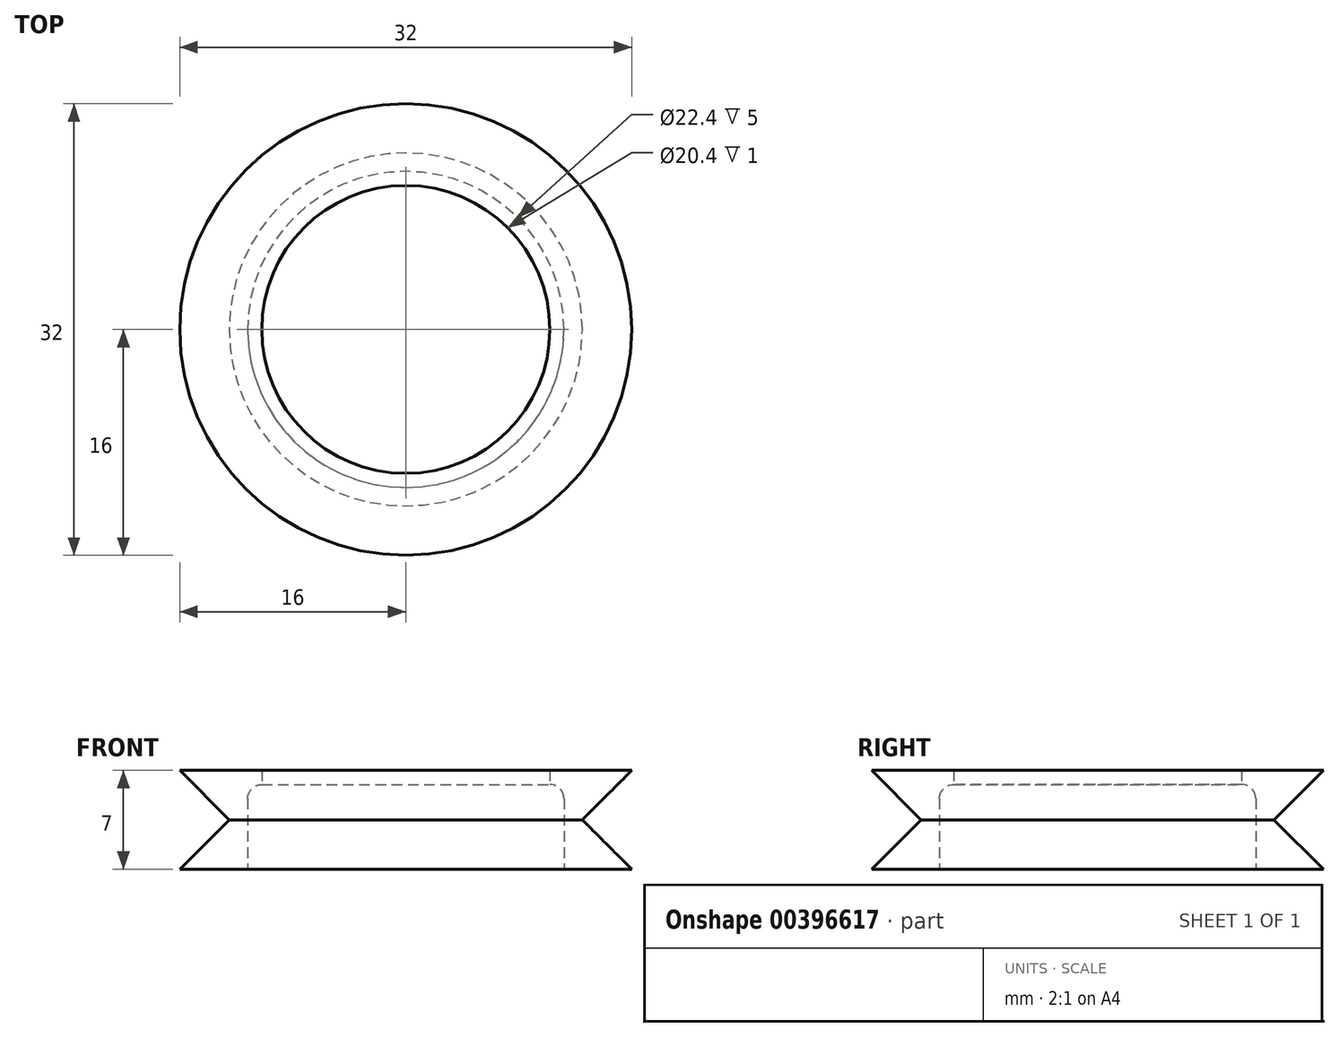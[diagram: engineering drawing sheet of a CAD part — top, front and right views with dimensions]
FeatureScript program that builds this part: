
annotation { "Feature Type Name" : "Feature", "Feature Type Description" : "" }
export const myFeature = defineFeature(function(context is Context, id is Id, definition is map)
    precondition{}
    {
        {
            var Q0;
            Q0=qCreatedBy(makeId("Front.planeOp"),FACE);
            var sketch = newSketch(context, id + "F0", { "sketchPlane" : qUnion([Q0])});
            skLineSegment(sketch, "E0.bottom", {"start": v(0, 13.24) * mm, "end": v(0, 13.24) * mm});
            skLineSegment(sketch, "E0.top", {"start": v(0, -13.74) * mm, "end": v(0, -13.74) * mm});
            skLineSegment(sketch, "E0.left", {"start": v(0, 13.24) * mm, "end": v(0, -13.74) * mm, "construction": true});
            skLineSegment(sketch, "E0.right", {"start": v(0, 13.24) * mm, "end": v(0, -13.74) * mm, "construction": true});
            skLineSegment(sketch, "E1.bottom", {"start": v(0, 3.5) * mm, "end": v(16, 3.5) * mm});
            skLineSegment(sketch, "E1.top", {"start": v(0, -3.5) * mm, "end": v(16, -3.5) * mm});
            skLineSegment(sketch, "E1.left", {"start": v(0, 3.5) * mm, "end": v(0, -3.5) * mm});
            skLineSegment(sketch, "E1.right", {"start": v(16, 3.5) * mm, "end": v(16, -3.5) * mm});
            skLineSegment(sketch, "E2", {"start": v(16, 3.5) * mm, "end": v(12.5, 0) * mm});
            skPoint(sketch, "E2.endSnap0", {"position": v(16, 0) * mm});
            skLineSegment(sketch, "E3", {"start": v(12.5, 0) * mm, "end": v(16, -3.5) * mm});
            skLineSegment(sketch, "E4", {"start": v(11.2, 3.5) * mm, "end": v(11.2, -3.5) * mm});
            skLineSegment(sketch, "E5", {"start": v(11.2, 2.5) * mm, "end": v(10.2, 2.5) * mm});
            skLineSegment(sketch, "E6", {"start": v(10.2, 3.5) * mm, "end": v(10.2, 2.5) * mm});
            skSolve(sketch);
        }
        {
            var Q0;
            {var subQ4=sQuery(id+"F0.wireOp",EDGE,"E2");Q0=makeQuery(id+"F0.imprint","IMPRINT",FACE,{"disambiguationData":[TD([[makeQuery(id+"F0.imprint","IMPRINT",EDGE,{"derivedFrom":subQ4}),-1.0]])]});}
            var Q1;
            {var subQ0=sQuery(id+"F0.wireOp",EDGE,"E1.left");Q1=makeQuery(id+"F0.imprint","IMPRINT",FACE,{"disambiguationData":[TD([[makeQuery(id+"F0.imprint","IMPRINT",EDGE,{"derivedFrom":subQ0}),1.0]])]});}
            var Q2;
            {var subQ4=sQuery(id+"F0.wireOp",EDGE,"E5");Q2=makeQuery(id+"F0.imprint","IMPRINT",FACE,{"disambiguationData":[TD([[makeQuery(id+"F0.imprint","IMPRINT",EDGE,{"derivedFrom":subQ4}),-1.0]])]});}
            var Q3;
            Q3=sQuery(id+"F0.wireOp",EDGE,"E0.right");
            revolve(context, id + "F1", {"entities" : qUnion([Q0, Q1, Q2]), "axis" : qUnion([Q3]), "revolveType" : RevolveType.FULL});
        }
        {
            var Q0;
            {var subQ0=sQuery(id+"F0.wireOp",EDGE,"E1.left");Q0=makeQuery(id+"F0.imprint","IMPRINT",FACE,{"disambiguationData":[TD([[makeQuery(id+"F0.imprint","IMPRINT",EDGE,{"derivedFrom":subQ0}),1.0]])]});}
            var Q1;
            Q1=sQuery(id+"F0.wireOp",EDGE,"E0.right");
            revolve(context, id + "F2", {"operationType" : NewBodyOperationType.REMOVE, "entities" : qUnion([Q0]), "axis" : qUnion([Q1]), "revolveType" : RevolveType.FULL, "oppositeDirection" : true});
        }
        {
            var Q0;
            Q0=makeQuery(id+"F2.boolean.opBoolean","COPY",EDGE,{"derivedFrom":makeQuery(id+"F2.opRevolve","SWEPT_EDGE",EDGE,{"disambiguationData":[OSD([sQuery(id+"F0.wireOp",EDGE,"E4"),sQuery(id+"F0.wireOp",EDGE,"E5")])]})});
            fillet(context, id + "F3", {"entities" : qUnion([Q0]), "radius" : 1 * mm, "tangentPropagation" : true, "allowEdgeOverflow" : false});
        }
    });
